# Revit family: eldinaaaaa
name_source: partatom
category: Lighting Fixtures
units: mm (PartAtom-declared; Revit-internal decimal feet)

## family parameters
Cut with Voids When Loaded = No
Host = Face
Light Source = No
OmniClass Number = 23.80.70.11
OmniClass Title = Luminaries for Internal Lighting
Part Type = Normal
Room Calculation Point = No
Round Connector Dimension = Use Diameter
Shared = No

## types (64) — shared parameters
Assembly Code = D5020200
Default Elevation = 48 "
Description = StarLink Wide
Distribution = SD-SatinIce Diffused
Edition number = 1
Electrical Disconnect = Yes
Frequency = 60 Hz
Height = 2.9 "
Keynote = 16500
Lamp = LED
Manufacturer = StarTek Lighting
Number of Poles = 3
Phase = 1
Photometric Note = Import IES files https://starteklightingamerica.com
Photometric Webfile Note = Please remember to reload the shared light file with the type catalog for all available light options and link the proper .ies file to the shared file.
Power Factor = 0.93
Product Guid = 08d8bbde-968b-462b-8ece-db3c3b62b9a7
Product data url = https://www.bimobject.com
Type Comments = Linear Lighting Fixture
URL = https://starteklightingamerica.com
Wattage Comments = Efficacy up to 155 lm/W
Width = 3 "
z_End = Run : End Fixture
z_Middle = Run : Middle Fixture
z_Standalone = Run : Standalone Fixture
z_Start = Run : Start Fixture

## per-type parameters (varying)
| type | Apparent Load | CRI | Input Wattage | Length | Model | Output | Photometric Option | Voltage | Voltage Range | Weight |
| SLW-8FT-High-SD-50K-90CRI-347V | 42 VA | 90 | 116 W | 48 " | SLW-8-H-SD-50K-90-__-__-C | High | Light-Source_StarTek_StarLink-Wide-Rotational-Mount : Not a Type - Load Type Catalog! | 347 V | 347V | 8.00 lbf |
| SLW-8FT-High-SD-50K-90CRI-120-277V | 42 VA | 90 | 116 W | 96 " | SLW-8-H-SD-50K-90-__-__-U | High | Light-Source_StarTek_StarLink-Wide-Rotational-Mount : Not a Type - Load Type Catalog! | 120 V | 120-277V | 16.00 lbf |
| SLW-8FT-High-SD-50K-80CRI-347V | 42 VA | 80 | 116 W | 96 " | SLW-8-H-SD-50K-80-__-__-C | High | Light-Source_StarTek_StarLink-Wide-Rotational-Mount : Not a Type - Load Type Catalog! | 347 V | 347V | 16.00 lbf |
| SLW-8FT-High-SD-50K-80CRI-120-277V | 42 VA | 80 | 116 W | 96 " | SLW-8-H-SD-50K-80-__-__-U | High | Light-Source_StarTek_StarLink-Wide-Rotational-Mount : Not a Type - Load Type Catalog! | 120 V | 120-277V | 16.00 lbf |
| SLW-8FT-High-SD-40K-90CRI-347V | 42 VA | 90 | 116 W | 96 " | SLW-8-H-SD-40K-90-__-__-C | High | Light-Source_StarTek_StarLink-Wide-Rotational-Mount : Not a Type - Load Type Catalog! | 347 V | 347V | 16.00 lbf |
| SLW-8FT-High-SD-40K-90CRI-120-277V | 42 VA | 90 | 116 W | 96 " | SLW-8-H-SD-40K-90-__-__-U | High | Light-Source_StarTek_StarLink-Wide-Rotational-Mount : Not a Type - Load Type Catalog! | 120 V | 120-277V | 16.00 lbf |
| SLW-8FT-High-SD-40K-80CRI-347V | 42 VA | 80 | 116 W | 96 " | SLW-8-H-SD-40K-80-__-__-C | High | Light-Source_StarTek_StarLink-Wide-Rotational-Mount : Not a Type - Load Type Catalog! | 347 V | 347V | 16.00 lbf |
| SLW-8FT-High-SD-40K-80CRI-120-277V | 42 VA | 80 | 116 W | 96 " | SLW-8-H-SD-40K-80-__-__-U | High | Light-Source_StarTek_StarLink-Wide-Rotational-Mount : Not a Type - Load Type Catalog! | 120 V | 120-277V | 16.00 lbf |
| SLW-8FT-High-SD-35K-90CRI-347V | 42 VA | 90 | 116 W | 96 " | SLW-8-H-SD-35K-90-__-__-C | High | Light-Source_StarTek_StarLink-Wide-Rotational-Mount : Not a Type - Load Type Catalog! | 347 V | 347V | 16.00 lbf |
| SLW-8FT-High-SD-35K-90CRI-120-277V | 42 VA | 90 | 116 W | 96 " | SLW-8-H-SD-35K-90-__-__-U | High | Light-Source_StarTek_StarLink-Wide-Rotational-Mount : Not a Type - Load Type Catalog! | 120 V | 120-277V | 16.00 lbf |
| SLW-8FT-High-SD-35K-80CRI-347V | 42 VA | 80 | 116 W | 96 " | SLW-8-H-SD-35K-80-__-__-C | High | Light-Source_StarTek_StarLink-Wide-Rotational-Mount : Not a Type - Load Type Catalog! | 347 V | 347V | 16.00 lbf |
| SLW-8FT-High-SD-35K-80CRI-120-277V | 42 VA | 80 | 116 W | 96 " | SLW-8-H-SD-35K-80-__-__-U | High | Light-Source_StarTek_StarLink-Wide-Rotational-Mount : Not a Type - Load Type Catalog! | 120 V | 120-277V | 16.00 lbf |
| SLW-8FT-High-SD-30K-90CRI-347V | 42 VA | 90 | 116 W | 96 " | SLW-8-H-SD-30K-90-__-__-C | High | Light-Source_StarTek_StarLink-Wide-Rotational-Mount : Not a Type - Load Type Catalog! | 347 V | 347V | 16.00 lbf |
| SLW-8FT-High-SD-30K-90CRI-120-277V | 42 VA | 90 | 116 W | 96 " | SLW-8-H-SD-30K-90-__-__-U | High | Light-Source_StarTek_StarLink-Wide-Rotational-Mount : Not a Type - Load Type Catalog! | 120 V | 120-277V | 16.00 lbf |
| SLW-8FT-High-SD-30K-80CRI-347V | 42 VA | 80 | 116 W | 96 " | SLW-8-H-SD-30K-80-__-__-C | High | Light-Source_StarTek_StarLink-Wide-Rotational-Mount : Not a Type - Load Type Catalog! | 347 V | 347V | 16.00 lbf |
| SLW-8FT-High-SD-30K-80CRI-120-277V | 42 VA | 80 | 116 W | 96 " | SLW-8-H-SD-30K-80-__-__-U | High | Light-Source_StarTek_StarLink-Wide-Rotational-Mount : Not a Type - Load Type Catalog! | 120 V | 120-277V | 16.00 lbf |
| SLW-8FT-Standard-SD-50K-90CRI-347V | 31 VA | 90 | 87 W | 96 " | SLW-8-S-SD-50K-90-__-__-C | Standard | Light-Source_StarTek_StarLink-Wide-Rotational-Mount : Not a Type - Load Type Catalog! | 347 V | 347V | 16.00 lbf |
| SLW-8FT-Standard-SD-50K-90CRI-120-277V | 31 VA | 90 | 87 W | 96 " | SLW-8-S-SD-50K-90-__-__-U | Standard | Light-Source_StarTek_StarLink-Wide-Rotational-Mount : Not a Type - Load Type Catalog! | 120 V | 120-277V | 16.00 lbf |
| SLW-8FT-Standard-SD-50K-80CRI-347V | 31 VA | 80 | 87 W | 96 " | SLW-8-S-SD-50K-80-__-__-C | Standard | Light-Source_StarTek_StarLink-Wide-Rotational-Mount : Not a Type - Load Type Catalog! | 347 V | 347V | 16.00 lbf |
| SLW-8FT-Standard-SD-50K-80CRI-120-277V | 31 VA | 80 | 87 W | 96 " | SLW-8-S-SD-50K-80-__-__-U | Standard | Light-Source_StarTek_StarLink-Wide-Rotational-Mount : Not a Type - Load Type Catalog! | 120 V | 120-277V | 16.00 lbf |
| SLW-8FT-Standard-SD-40K-90CRI-347V | 31 VA | 90 | 87 W | 96 " | SLW-8-S-SD-40K-90-__-__-C | Standard | Light-Source_StarTek_StarLink-Wide-Rotational-Mount : Not a Type - Load Type Catalog! | 347 V | 347V | 16.00 lbf |
| SLW-8FT-Standard-SD-40K-90CRI-120-277V | 31 VA | 90 | 87 W | 96 " | SLW-8-S-SD-40K-90-__-__-U | Standard | Light-Source_StarTek_StarLink-Wide-Rotational-Mount : Not a Type - Load Type Catalog! | 120 V | 120-277V | 16.00 lbf |
| SLW-8FT-Standard-SD-40K-80CRI-347V | 31 VA | 80 | 87 W | 96 " | SLW-8-S-SD-40K-80-__-__-C | Standard | Light-Source_StarTek_StarLink-Wide-Rotational-Mount : Not a Type - Load Type Catalog! | 347 V | 347V | 16.00 lbf |
| SLW-8FT-Standard-SD-40K-80CRI-120-277V | 31 VA | 80 | 87 W | 96 " | SLW-8-S-SD-40K-80-__-__-U | Standard | Light-Source_StarTek_StarLink-Wide-Rotational-Mount : SLW-8FT-Standard-SD-40K | 120 V | 120-277V | 16.00 lbf |
| SLW-8FT-Standard-SD-35K-90CRI-347V | 31 VA | 90 | 87 W | 96 " | SLW-8-S-SD-35K-90-__-__-C | Standard | Light-Source_StarTek_StarLink-Wide-Rotational-Mount : Not a Type - Load Type Catalog! | 347 V | 347V | 16.00 lbf |
| SLW-8FT-Standard-SD-35K-90CRI-120-277V | 31 VA | 90 | 87 W | 96 " | SLW-8-S-SD-35K-90-__-__-U | Standard | Light-Source_StarTek_StarLink-Wide-Rotational-Mount : Not a Type - Load Type Catalog! | 120 V | 120-277V | 16.00 lbf |
| SLW-8FT-Standard-SD-35K-80CRI-347V | 31 VA | 80 | 87 W | 96 " | SLW-8-S-SD-35K-80-__-__-C | Standard | Light-Source_StarTek_StarLink-Wide-Rotational-Mount : Not a Type - Load Type Catalog! | 347 V | 347V | 16.00 lbf |
| SLW-8FT-Standard-SD-35K-80CRI-120-277V | 31 VA | 80 | 87 W | 96 " | SLW-8-S-SD-35K-80-__-__-U | Standard | Light-Source_StarTek_StarLink-Wide-Rotational-Mount : Not a Type - Load Type Catalog! | 120 V | 120-277V | 16.00 lbf |
| SLW-8FT-Standard-SD-30K-90CRI-347V | 31 VA | 90 | 87 W | 96 " | SLW-8-S-SD-30K-90-__-__-C | Standard | Light-Source_StarTek_StarLink-Wide-Rotational-Mount : Not a Type - Load Type Catalog! | 347 V | 347V | 16.00 lbf |
| SLW-8FT-Standard-SD-30K-90CRI-120-277V | 31 VA | 90 | 87 W | 96 " | SLW-8-S-SD-30K-90-__-__-U | Standard | Light-Source_StarTek_StarLink-Wide-Rotational-Mount : Not a Type - Load Type Catalog! | 120 V | 120-277V | 16.00 lbf |
| SLW-8FT-Standard-SD-30K-80CRI-347V | 31 VA | 80 | 87 W | 96 " | SLW-8-S-SD-30K-80-__-__-C | Standard | Light-Source_StarTek_StarLink-Wide-Rotational-Mount : Not a Type - Load Type Catalog! | 347 V | 347V | 16.00 lbf |
| SLW-8FT-Standard-SD-30K-80CRI-120-277V | 31 VA | 80 | 87 W | 96 " | SLW-8-S-SD-30K-80-__-__-U | Standard | Light-Source_StarTek_StarLink-Wide-Rotational-Mount : Not a Type - Load Type Catalog! | 120 V | 120-277V | 16.00 lbf |
| SLW-4FT-High-SD-50K-90CRI-347V | 32 VA | 90 | 90 W | 48 " | SLW-4-H-SD-50K-90-__-__-C | High | Light-Source_StarTek_StarLink-Wide-Rotational-Mount : Not a Type - Load Type Catalog! | 347 V | 347V | 8.00 lbf |
| SLW-4FT-High-SD-50K-90CRI-120-277V | 32 VA | 90 | 90 W | 48 " | SLW-4-H-SD-50K-90-__-__-U | High | Light-Source_StarTek_StarLink-Wide-Rotational-Mount : Not a Type - Load Type Catalog! | 120 V | 120-277V | 8.00 lbf |
| SLW-4FT-High-SD-50K-80CRI-347V | 32 VA | 80 | 90 W | 48 " | SLW-4-H-SD-50K-80-__-__-C | High | Light-Source_StarTek_StarLink-Wide-Rotational-Mount : Not a Type - Load Type Catalog! | 347 V | 347V | 8.00 lbf |
| SLW-4FT-High-SD-50K-80CRI-120-277V | 32 VA | 80 | 90 W | 48 " | SLW-4-H-SD-50K-80-__-__-U | High | Light-Source_StarTek_StarLink-Wide-Rotational-Mount : Not a Type - Load Type Catalog! | 120 V | 120-277V | 8.00 lbf |
| SLW-4FT-High-SD-40K-90CRI-347V | 32 VA | 90 | 90 W | 48 " | SLW-4-H-SD-40K-90-__-__-C | High | Light-Source_StarTek_StarLink-Wide-Rotational-Mount : Not a Type - Load Type Catalog! | 347 V | 347V | 8.00 lbf |
| SLW-4FT-High-SD-40K-90CRI-120-277V | 32 VA | 90 | 90 W | 48 " | SLW-4-H-SD-40K-90-__-__-U | High | Light-Source_StarTek_StarLink-Wide-Rotational-Mount : Not a Type - Load Type Catalog! | 120 V | 120-277V | 8.00 lbf |
| SLW-4FT-High-SD-40K-80CRI-347V | 32 VA | 80 | 90 W | 48 " | SLW-4-H-SD-40K-80-__-__-C | High | Light-Source_StarTek_StarLink-Wide-Rotational-Mount : Not a Type - Load Type Catalog! | 347 V | 347V | 8.00 lbf |
| SLW-4FT-High-SD-40K-80CRI-120-277V | 32 VA | 80 | 90 W | 48 " | SLW-4-H-SD-40K-80-__-__-U | High | Light-Source_StarTek_StarLink-Wide-Rotational-Mount : Not a Type - Load Type Catalog! | 120 V | 120-277V | 8.00 lbf |
| SLW-4FT-High-SD-35K-90CRI-347V | 32 VA | 90 | 90 W | 48 " | SLW-4-H-SD-35K-90-__-__-C | High | Light-Source_StarTek_StarLink-Wide-Rotational-Mount : Not a Type - Load Type Catalog! | 347 V | 347V | 8.00 lbf |
| SLW-4FT-High-SD-35K-90CRI-120-277V | 32 VA | 90 | 90 W | 48 " | SLW-4-H-SD-35K-90-__-__-U | High | Light-Source_StarTek_StarLink-Wide-Rotational-Mount : Not a Type - Load Type Catalog! | 120 V | 120-277V | 8.00 lbf |
| SLW-4FT-High-SD-35K-80CRI-347V | 32 VA | 80 | 90 W | 48 " | SLW-4-H-SD-35K-80-__-__-C | High | Light-Source_StarTek_StarLink-Wide-Rotational-Mount : Not a Type - Load Type Catalog! | 347 V | 347V | 8.00 lbf |
| SLW-4FT-High-SD-35K-80CRI-120-277V | 32 VA | 80 | 90 W | 48 " | SLW-4-H-SD-35K-80-__-__-U | High | Light-Source_StarTek_StarLink-Wide-Rotational-Mount : Not a Type - Load Type Catalog! | 120 V | 120-277V | 8.00 lbf |
| SLW-4FT-High-SD-30K-90CRI-347V | 32 VA | 90 | 90 W | 48 " | SLW-4-H-SD-30K-90-__-__-C | High | Light-Source_StarTek_StarLink-Wide-Rotational-Mount : Not a Type - Load Type Catalog! | 347 V | 347V | 8.00 lbf |
| SLW-4FT-High-SD-30K-90CRI-120-277V | 32 VA | 90 | 90 W | 48 " | SLW-4-H-SD-30K-90-__-__-U | High | Light-Source_StarTek_StarLink-Wide-Rotational-Mount : Not a Type - Load Type Catalog! | 120 V | 120-277V | 8.00 lbf |
| SLW-4FT-High-SD-30K-80CRI-347V | 32 VA | 80 | 90 W | 48 " | SLW-4-H-SD-30K-80-__-__-C | High | Light-Source_StarTek_StarLink-Wide-Rotational-Mount : Not a Type - Load Type Catalog! | 347 V | 347V | 8.00 lbf |
| SLW-4FT-High-SD-30K-80CRI-120-277V | 32 VA | 80 | 90 W | 48 " | SLW-4-H-SD-30K-80-__-__-U | High | Light-Source_StarTek_StarLink-Wide-Rotational-Mount : Not a Type - Load Type Catalog! | 120 V | 120-277V | 8.00 lbf |
| SLW-4FT-Standard-SD-50K-90CRI-347V | 17 VA | 90 | 47 W | 48 " | SLW-4-S-SD-50K-90-__-__-C | Standard | Light-Source_StarTek_StarLink-Wide-Rotational-Mount : Not a Type - Load Type Catalog! | 347 V | 347V | 8.00 lbf |
| SLW-4FT-Standard-SD-50K-90CRI-120-277V | 17 VA | 90 | 47 W | 48 " | SLW-4-S-SD-50K-90-__-__-U | Standard | Light-Source_StarTek_StarLink-Wide-Rotational-Mount : Not a Type - Load Type Catalog! | 120 V | 120-277V | 8.00 lbf |
| SLW-4FT-Standard-SD-50K-80CRI-347V | 17 VA | 80 | 47 W | 48 " | SLW-4-S-SD-50K-80-__-__-C | Standard | Light-Source_StarTek_StarLink-Wide-Rotational-Mount : Not a Type - Load Type Catalog! | 347 V | 347V | 8.00 lbf |
| SLW-4FT-Standard-SD-50K-80CRI-120-277V | 17 VA | 80 | 47 W | 48 " | SLW-4-S-SD-50K-80-__-__-U | Standard | Light-Source_StarTek_StarLink-Wide-Rotational-Mount : Not a Type - Load Type Catalog! | 120 V | 120-277V | 8.00 lbf |
| SLW-4FT-Standard-SD-40K-90CRI-347V | 17 VA | 90 | 47 W | 48 " | SLW-4-S-SD-40K-90-__-__-C | Standard | Light-Source_StarTek_StarLink-Wide-Rotational-Mount : Not a Type - Load Type Catalog! | 347 V | 347V | 8.00 lbf |
| SLW-4FT-Standard-SD-40K-90CRI-120-277V | 17 VA | 90 | 47 W | 48 " | SLW-4-S-SD-40K-90-__-__-U | Standard | Light-Source_StarTek_StarLink-Wide-Rotational-Mount : Not a Type - Load Type Catalog! | 120 V | 120-277V | 8.00 lbf |
| SLW-4FT-Standard-SD-40K-80CRI-347V | 17 VA | 80 | 47 W | 48 " | SLW-4-S-SD-40K-80-__-__-C | Standard | Light-Source_StarTek_StarLink-Wide-Rotational-Mount : Not a Type - Load Type Catalog! | 347 V | 347V | 8.00 lbf |
| SLW-4FT-Standard-SD-40K-80CRI-120-277V | 17 VA | 80 | 47 W | 48 " | SLW-4-S-SD-40K-80-__-__-U | Standard | Light-Source_StarTek_StarLink-Wide-Rotational-Mount : Not a Type - Load Type Catalog! | 120 V | 120-277V | 8.00 lbf |
| SLW-4FT-Standard-SD-35K-90CRI-347V | 17 VA | 90 | 47 W | 48 " | SLW-4-S-SD-35K-90-__-__-C | Standard | Light-Source_StarTek_StarLink-Wide-Rotational-Mount : Not a Type - Load Type Catalog! | 347 V | 347V | 8.00 lbf |
| SLW-4FT-Standard-SD-35K-90CRI-120-277V | 17 VA | 90 | 47 W | 48 " | SLW-4-S-SD-35K-90-__-__-U | Standard | Light-Source_StarTek_StarLink-Wide-Rotational-Mount : Not a Type - Load Type Catalog! | 120 V | 120-277V | 8.00 lbf |
| SLW-4FT-Standard-SD-35K-80CRI-347V | 17 VA | 80 | 47 W | 48 " | SLW-4-S-SD-35K-80-__-__-C | Standard | Light-Source_StarTek_StarLink-Wide-Rotational-Mount : Not a Type - Load Type Catalog! | 347 V | 347V | 8.00 lbf |
| SLW-4FT-Standard-SD-35K-80CRI-120-277V | 17 VA | 80 | 47 W | 48 " | SLW-4-S-SD-35K-80-__-__-U | Standard | Light-Source_StarTek_StarLink-Wide-Rotational-Mount : Not a Type - Load Type Catalog! | 120 V | 120-277V | 8.00 lbf |
| SLW-4FT-Standard-SD-30K-90CRI-347V | 17 VA | 90 | 47 W | 48 " | SLW-4-S-SD-30K-90-__-__-C | Standard | Light-Source_StarTek_StarLink-Wide-Rotational-Mount : Not a Type - Load Type Catalog! | 347 V | 347V | 8.00 lbf |
| SLW-4FT-Standard-SD-30K-90CRI-120-277V | 17 VA | 90 | 47 W | 48 " | SLW-4-S-SD-30K-90-__-__-U | Standard | Light-Source_StarTek_StarLink-Wide-Rotational-Mount : Not a Type - Load Type Catalog! | 120 V | 120-277V | 8.00 lbf |
| SLW-4FT-Standard-SD-30K-80CRI-347V | 17 VA | 80 | 47 W | 48 " | SLW-4-S-SD-30K-80-__-__-C | Standard | Light-Source_StarTek_StarLink-Wide-Rotational-Mount : Not a Type - Load Type Catalog! | 347 V | 347V | 8.00 lbf |
| SLW-4FT-Standard-SD-30K-80CRI-120-277V | 17 VA | 80 | 47 W | 48 " | SLW-4-S-SD-30K-80-__-__-U | Standard | Light-Source_StarTek_StarLink-Wide-Rotational-Mount : Not a Type - Load Type Catalog! | 120 V | 120-277V | 8.00 lbf |

## geometry (parser evidence)
native form markers: Sweep x12
no freeform markers — native parametric forms only
